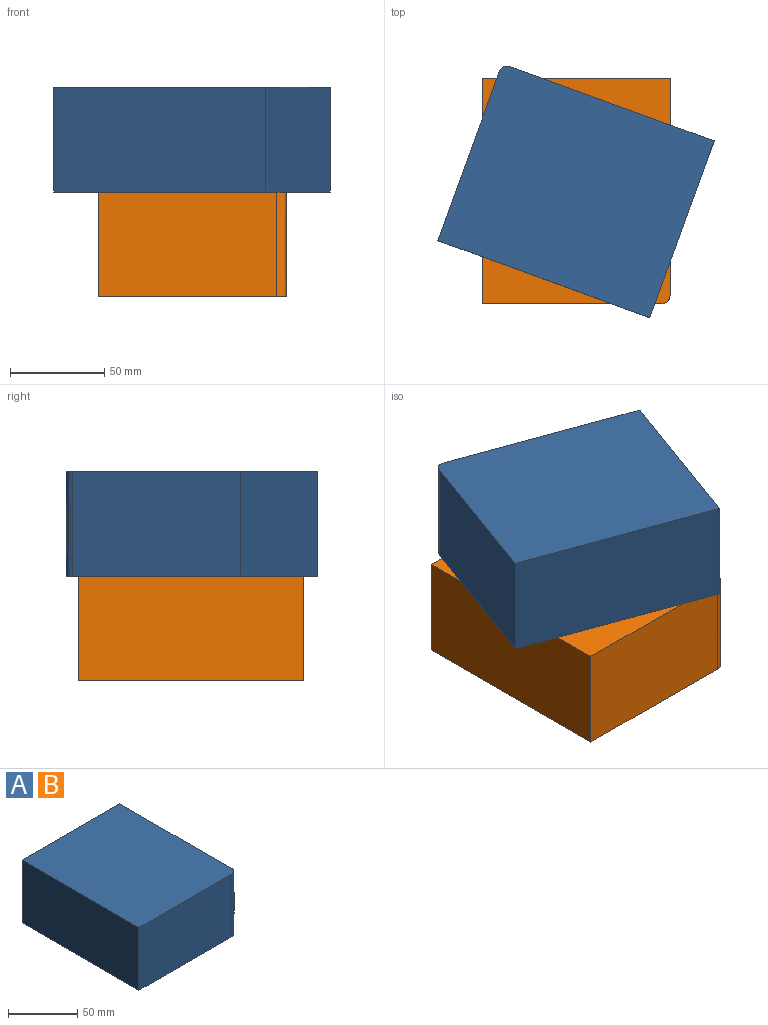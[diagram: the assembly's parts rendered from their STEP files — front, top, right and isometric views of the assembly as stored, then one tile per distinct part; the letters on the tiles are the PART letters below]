
ASSEMBLY  parts=2 mates=1
PART A: 7 faces, bbox 99.5x119.3x60.9 mm
  f0: plane 99.49x55.37mm, normal (0,1,0), area 5508.8mm2, adj f1,f3,f4,f5
  f1: plane 119.33x55.37mm, normal (-1,0,0), area 6607.3mm2, adj f0,f2,f4,f5
  f2: plane 94.41x55.37mm, normal (0,-1,0), area 5227.5mm2, adj f1,f4,f5,f6
  f3: plane 114.25x55.37mm, normal (1,0,0), area 6326.1mm2, adj f0,f4,f5,f6
  f4: plane 119.33x99.49mm, normal (0,0,1), area 11867.1mm2, adj f0,f1,f2,f3,f6
  f5: plane 119.33x99.49mm, normal (0,0,-1), area 11867.1mm2, adj f0,f1,f2,f3,f6
  f6: bspline ~60.91x5.08mm, area 456.6mm2, adj f2,f3,f4,f5
PART B: same geometry as A
PLACE A rot(axis=(0.82,0.57,0),180deg) t=(-93.12,6.24,95.96)mm
PLACE B t=(-27.17,-87.95,-14.79)mm
MATE revolute A.f4 <-> B.f4  axis (0,0,-1) through (-115.34,-79.5,40.59)mm
